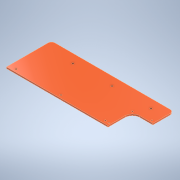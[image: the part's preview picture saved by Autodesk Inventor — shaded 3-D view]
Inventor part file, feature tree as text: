
AUTODESK INVENTOR PART (.ipt)
format: ipt  version: 2021 (Build 250183000, 183)  size: 152,576 bytes
history: native  units: mm
features: sketch x4, extrude x2, hole x2
ambient origin geometry x8: Origin, YZ Plane, XZ Plane, XY Plane, X Axis, Y Axis, Z Axis, Center Point
bodies: Solid1 (feature_tree)
feature tree (8):
  extrude  "Extrusion1"  Depth=92.25mm
  hole  "Hole1"  [1 undecoded]
  extrude  "Extrusion2"  Depth=6.0mm
  hole  "Hole2"  [1 undecoded]
  sketch  "Sketch1"  dims[d0=250.0mm d1=92.25mm]
  sketch  "Sketch2"  dims[d2=7.0mm d3=3.0mm d4=0.0mm]
  sketch  "Sketch3"  dims[d5=18.25mm d6=6.0mm]
  sketch  "Sketch4"  dims[d8=80.0mm d9=80.0mm d13=3.8mm d14=6.0mm d15=4.0mm d16=2.0mm d17=90.0deg d18=8.0mm d19=20.594885mm d20=13.5mm d22=196.5mm d23=62.0mm d24=105.5mm d26=50.0mm d27=208.0mm d28=15.0mm d29=0.0mm d30=0.0mm d31=4.0mm d32=4.0mm d33=6.0mm d34=6.0mm d35=18.0mm d36=18.0mm d37=3.2mm d38=6.0mm d39=4.0mm d40=2.0mm d41=90.0deg d42=8.0mm d43=20.594885mm]
note: 2 required parameter values undecoded (feature->parameter linkage not recoverable at this tier; creation-order binding heuristic only, values carry confidence <= 0.55)
